# Revit family: HOSPIVAC V3 E25-40
name_source: partatom
category: Equipement de génie climatique
revit_build: Autodesk Revit 2018 (Build: 20170223_1515(x64)
units: mm (PartAtom-declared; Revit-internal decimal feet)

## family parameters
Basée sur le plan de construction = Non
Classification = Aucun
Cote de connecteur circulaire = Utiliser le diamètre
Couper avec des vides une fois chargée = Non
Partagée = Non
Point de calcul de pièce = Non
Toujours verticalement = Oui
Type d'élément = Normal

## types (2) — shared parameters
COS_PHI = 0.9
DESCR_ALIM_X = Alimentation X ; 5G1.5mm²
DESCR_ALIM_Y = Alimentation Y ; 5G1.5mm²
DESCR_RESERV = Aspiration Réservoir ; G 1" MAL
DIAM_ASPI_VIDE = 25 mm  [stored 0.082021 ft]
DIAM_REFOUL_VIDE = 25 mm  [stored 0.082021 ft]
DOUBLE_ALIMENTATION = Oui
FREQUENCE = 50 Hz
Fabricant = MIL'S
HAUTEUR = 1375 mm  [stored 4.51115 ft]
LARGEUR = 600 mm  [stored 1.9685 ft]
LONGUEUR = 784 mm  [stored 2.57218 ft]
Lien espace client = https://www.mils.fr
Modèle = HOSPIVAC V3 EVISA
NBR_POLES = 3
NEUTRE = Oui
OFFSET_HAUT_FILTR_1 = 970 mm  [stored 3.18241 ft]
OFFSET_HAUT_FILT_2 = 671 mm  [stored 2.20144 ft]
OFFSET_LONG_ASPI = 161 mm  [stored 0.528215 ft]
OFFSET_LONG_TE = 116 mm  [stored 0.380577 ft]
PROTEC_ELECT_X = Disjoncteur courbe D - 4A
PUISS_ELECT_X = 1 kW
PUISS_ELECT_Y = 2 kW
TENSION_ALIM = 400 V
TERRE = Oui
ØCANA = 35 mm  [stored 0.114829 ft]

## per-type parameters (varying)
| type | DEBIT_ASPI_VIDE | DEBIT_REFOUL_VIDE | DEGAG_CALORIFIQUE(kJ/h) | DESCR_APSI | DESCR_REFOUL | NIVEAU_SONORE(dB(A)) | OFFSET_HAUT_BOCAL_1 | OFFSET_HAUT_BOCAL_2 | POIDS(Kg) | PROTEC_ELECT_Y | PUISS_APPARENTE_X | PUISS_APPARENTE_Y | TYPE FILTRATION | TYPE_PPE | Zone de maintenance 1 | aaaa |
| HOSPIVAC V3 E25 | 84.0 m³/h | 84.0 m³/h | 9302 | Aspiration Vide ; 3x28 m³/h ; G 1" FEM | Refoulement Vide ; 3x28 m³/h ; G 1" MAL | 59 | 794 mm  [stored 2.60499 ft] | 495 mm  [stored 1.62402 ft] | 185 mm  [stored 0.606955 ft] | Disjoncteur courbe D - 6A | 833 VA | 1667 VA | FILTRATION ANTI-BACTERIENNE : FD30 | EVISA : b - E25.R | Oui | 1826 mm |
| HOSPIVAC V3 E40 | 132.0 m³/h | 132.0 m³/h | 13643 | Aspiration Vide ; 3x44 m³/h ; G 1" FEM | Refoulement Vide ; 3x44 m³/h ; G 1" MAL | 58 | 670 mm  [stored 2.19816 ft] | 371 mm  [stored 1.21719 ft] | 215 mm | Disjoncteur courbe D - 10A | 1222 VA | 2444 VA | FILTRATION ANTI-BACTERIENNE : FD65 | EVISA : d - E40.R | Non | 1820 mm |

note: [stored X ft] marks values corroborated as IEEE doubles in the binary element streams (Revit-internal decimal feet)

## geometry (parser evidence)
native form markers: Sweep x6
no freeform markers — native parametric forms only
